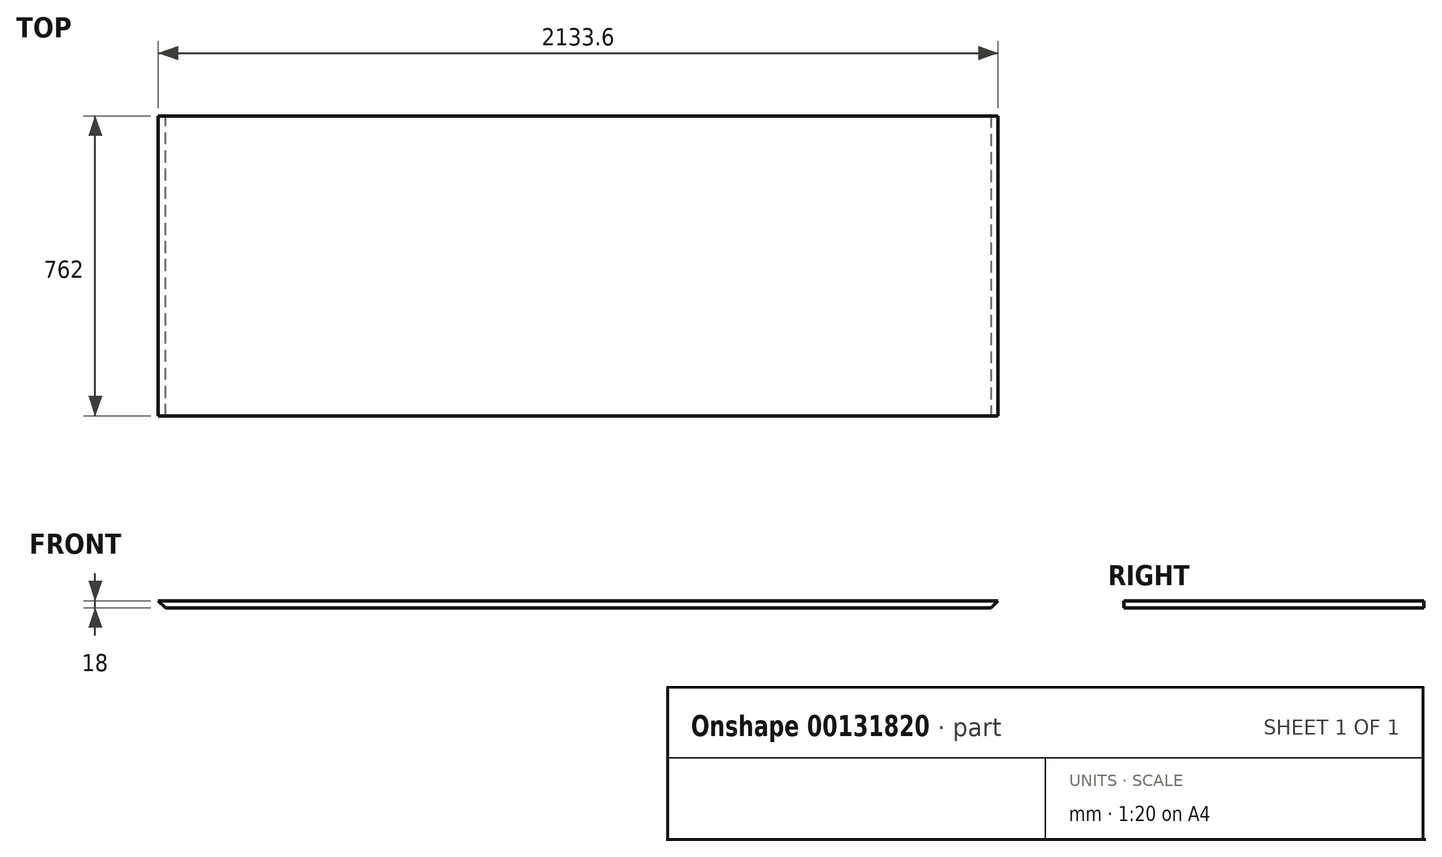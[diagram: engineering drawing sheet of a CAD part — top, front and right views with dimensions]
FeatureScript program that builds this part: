
annotation { "Feature Type Name" : "Feature", "Feature Type Description" : "" }
export const myFeature = defineFeature(function(context is Context, id is Id, definition is map)
    precondition{}
    {
        {
            var Q0;
            Q0=qCreatedBy(makeId("Top.planeOp"),FACE);
            var sketch = newSketch(context, id + "F0", { "sketchPlane" : qUnion([Q0])});
            skLineSegment(sketch, "E0.bottom", {"start": v(0, 0) * mm, "end": v(2133.6, 0) * mm});
            skLineSegment(sketch, "E0.top", {"start": v(0, 762) * mm, "end": v(2133.6, 762) * mm});
            skLineSegment(sketch, "E0.left", {"start": v(0, 0) * mm, "end": v(0, 762) * mm});
            skLineSegment(sketch, "E0.right", {"start": v(2133.6, 0) * mm, "end": v(2133.6, 762) * mm});
            skSolve(sketch);
        }
        {
            var Q0;
            Q0 = qSketchRegion(id + "F0", true);
            extrude(context, id + "F1", {"entities" : qUnion([Q0]), "oppositeDirection" : true, "depth" : 18 * mm});
        }
        {
            var Q0;
            Q0=makeQuery(id+"F1.opExtrude","CAP_EDGE",EDGE,{"disambiguationData":[OSD([sQuery(id+"F0.wireOp",EDGE,"E0.right")])],"isStart":false});
            var Q1;
            Q1=makeQuery(id+"F1.opExtrude","CAP_EDGE",EDGE,{"disambiguationData":[OSD([sQuery(id+"F0.wireOp",EDGE,"E0.left")])],"isStart":false});
            chamfer(context, id + "F2", {"entities" : qUnion([Q0, Q1]), "width" : 18 * mm, "tangentPropagation" : true});
        }
    });
